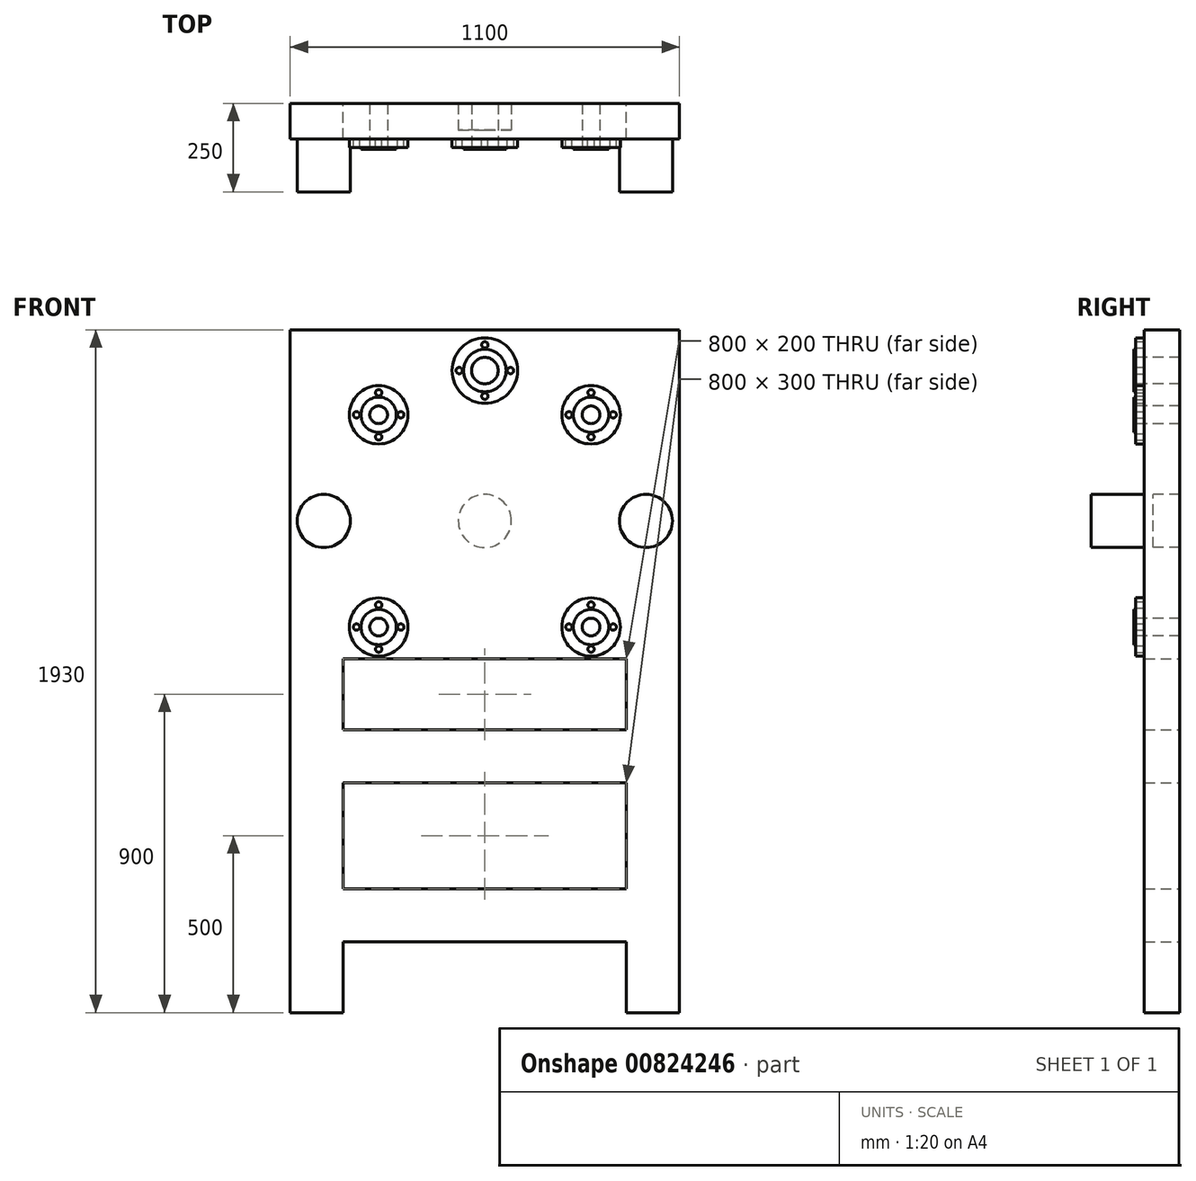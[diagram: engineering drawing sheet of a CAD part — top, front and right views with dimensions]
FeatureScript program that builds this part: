
annotation { "Feature Type Name" : "Feature", "Feature Type Description" : "" }
export const myFeature = defineFeature(function(context is Context, id is Id, definition is map)
    precondition{}
    {
        {
            var Q0;
            Q0=qCreatedBy(makeId("Front.planeOp"),FACE);
            var sketch = newSketch(context, id + "F0", { "sketchPlane" : qUnion([Q0])});
            skLineSegment(sketch, "E0.bottom", {"start": v(550, -965) * mm, "end": v(400, -965) * mm});
            skLineSegment(sketch, "E0.top", {"start": v(550, 965) * mm, "end": v(-550, 965) * mm});
            skLineSegment(sketch, "E0.left", {"start": v(550, -965) * mm, "end": v(550, 965) * mm});
            skLineSegment(sketch, "E0.right", {"start": v(-550, -965) * mm, "end": v(-550, 965) * mm});
            skPoint(sketch, "E0.middle", {"position": v(0, 0) * mm});
            skLineSegment(sketch, "E1.top", {"start": v(-400, -765) * mm, "end": v(400, -765) * mm});
            skLineSegment(sketch, "E1.left", {"start": v(-400, -965) * mm, "end": v(-400, -765) * mm});
            skLineSegment(sketch, "E1.right", {"start": v(400, -965) * mm, "end": v(400, -765) * mm});
            skLineSegment(sketch, "E2.bottom", {"start": v(-400, -615) * mm, "end": v(400, -615) * mm});
            skLineSegment(sketch, "E2.top", {"start": v(-400, -315) * mm, "end": v(400, -315) * mm});
            skLineSegment(sketch, "E2.left", {"start": v(-400, -615) * mm, "end": v(-400, -315) * mm});
            skLineSegment(sketch, "E2.right", {"start": v(400, -615) * mm, "end": v(400, -315) * mm});
            skLineSegment(sketch, "E3.trimOffspring", {"start": v(-400, -965) * mm, "end": v(-550, -965) * mm});
            skLineSegment(sketch, "E4.bottom", {"start": v(-400, -165) * mm, "end": v(400, -165) * mm});
            skLineSegment(sketch, "E4.top", {"start": v(-400, 35) * mm, "end": v(400, 35) * mm});
            skLineSegment(sketch, "E4.left", {"start": v(-400, -165) * mm, "end": v(-400, 35) * mm});
            skLineSegment(sketch, "E4.right", {"start": v(400, -165) * mm, "end": v(400, 35) * mm});
            skPoint(sketch, "E5.middle", {"position": v(0, 425) * mm});
            skSolve(sketch);
        }
        {
            var Q0;
            Q0=makeQuery(id+"F0.imprint","IMPRINT",FACE,{"disambiguationData":[TD([[makeQuery(id+"F0.imprint","IMPRINT",EDGE,{"derivedFrom":sQuery(id+"F0.wireOp",EDGE,"E0.bottom")}),-1.0]])]});
            extrude(context, id + "F1", {"entities" : qUnion([Q0]), "depth" : 100 * mm, "offsetDistance" : 25 * mm});
        }
        {
            var Q0;
            Q0=makeQuery(id+"F1.opExtrude","CAP_FACE",FACE,{"disambiguationData":[OSD([sQuery(id+"F0.wireOp",EDGE,"E0.bottom"),sQuery(id+"F0.wireOp",EDGE,"E0.top"),sQuery(id+"F0.wireOp",EDGE,"E0.left"),sQuery(id+"F0.wireOp",EDGE,"E0.right"),sQuery(id+"F0.wireOp",EDGE,"E1.top"),sQuery(id+"F0.wireOp",EDGE,"E1.left"),sQuery(id+"F0.wireOp",EDGE,"E1.right"),sQuery(id+"F0.wireOp",EDGE,"E2.bottom"),sQuery(id+"F0.wireOp",EDGE,"E2.top"),sQuery(id+"F0.wireOp",EDGE,"E2.left"),sQuery(id+"F0.wireOp",EDGE,"E2.right"),sQuery(id+"F0.wireOp",EDGE,"E3.trimOffspring"),sQuery(id+"F0.wireOp",EDGE,"nSGubIzk-R7de-6MO4-penA-cvBglKJnvsGC"),sQuery(id+"F0.wireOp",EDGE,"E4.bottom"),sQuery(id+"F0.wireOp",EDGE,"E4.top"),sQuery(id+"F0.wireOp",EDGE,"E4.left"),sQuery(id+"F0.wireOp",EDGE,"E4.right")])],"isStart":false});
            var sketch = newSketch(context, id + "F2", { "sketchPlane" : qUnion([Q0])});
            skCircle(sketch, "E6", {"center": v(-300, 125) * mm, "radius": 25 * mm});
            skCircle(sketch, "E7.0", {"center": v(0, 425) * mm, "radius": 75 * mm});
            skCircle(sketch, "E8.0.1.0", {"center": v(-300, 725) * mm, "radius": 25 * mm});
            skCircle(sketch, "E8.1.0.0", {"center": v(300, 125) * mm, "radius": 25 * mm});
            skCircle(sketch, "E8.1.1.0", {"center": v(300, 725) * mm, "radius": 25 * mm});
            skLineSegment(sketch, "E8.direction1", {"start": v(-300, 125) * mm, "end": v(300, 125) * mm, "construction": true});
            skLineSegment(sketch, "E8.direction2", {"start": v(-300, 125) * mm, "end": v(-300, 725) * mm, "construction": true});
            skSolve(sketch);
        }
        {
            var Q0;
            Q0 = qSketchRegion(id + "F2", true);
            extrude(context, id + "F3", {"entities" : qUnion([Q0]), "operationType" : NewBodyOperationType.REMOVE, "oppositeDirection" : true, "depth" : 100 * mm, "offsetDistance" : 25 * mm});
        }
        {
            var Q0;
            Q0=makeQuery(id+"F1.opExtrude","CAP_FACE",FACE,{"disambiguationData":[OSD([sQuery(id+"F0.wireOp",EDGE,"E0.bottom"),sQuery(id+"F0.wireOp",EDGE,"E0.top"),sQuery(id+"F0.wireOp",EDGE,"E0.left"),sQuery(id+"F0.wireOp",EDGE,"E0.right"),sQuery(id+"F0.wireOp",EDGE,"E1.top"),sQuery(id+"F0.wireOp",EDGE,"E1.left"),sQuery(id+"F0.wireOp",EDGE,"E1.right"),sQuery(id+"F0.wireOp",EDGE,"E2.bottom"),sQuery(id+"F0.wireOp",EDGE,"E2.top"),sQuery(id+"F0.wireOp",EDGE,"E2.left"),sQuery(id+"F0.wireOp",EDGE,"E2.right"),sQuery(id+"F0.wireOp",EDGE,"E3.trimOffspring"),sQuery(id+"F0.wireOp",EDGE,"nSGubIzk-R7de-6MO4-penA-cvBglKJnvsGC"),sQuery(id+"F0.wireOp",EDGE,"E4.bottom"),sQuery(id+"F0.wireOp",EDGE,"E4.top"),sQuery(id+"F0.wireOp",EDGE,"E4.left"),sQuery(id+"F0.wireOp",EDGE,"E4.right")])],"isStart":false});
            var sketch = newSketch(context, id + "F4", { "sketchPlane" : qUnion([Q0])});
            skCircle(sketch, "E9", {"center": v(-455, 425) * mm, "radius": 75 * mm});
            skCircle(sketch, "E10.MirrorC", {"center": v(455, 425) * mm, "radius": 75 * mm});
            skSolve(sketch);
        }
        {
            var Q0;
            Q0 = qSketchRegion(id + "F4", true);
            extrude(context, id + "F5", {"entities" : qUnion([Q0]), "operationType" : NewBodyOperationType.ADD, "depth" : 150 * mm, "offsetDistance" : 25 * mm});
        }
        {
            var Q0;
            Q0=makeQuery(id+"F1.opExtrude","CAP_FACE",FACE,{"disambiguationData":[OSD([sQuery(id+"F0.wireOp",EDGE,"E0.bottom"),sQuery(id+"F0.wireOp",EDGE,"E0.top"),sQuery(id+"F0.wireOp",EDGE,"E0.left"),sQuery(id+"F0.wireOp",EDGE,"E0.right"),sQuery(id+"F0.wireOp",EDGE,"E1.top"),sQuery(id+"F0.wireOp",EDGE,"E1.left"),sQuery(id+"F0.wireOp",EDGE,"E1.right"),sQuery(id+"F0.wireOp",EDGE,"E2.bottom"),sQuery(id+"F0.wireOp",EDGE,"E2.top"),sQuery(id+"F0.wireOp",EDGE,"E2.left"),sQuery(id+"F0.wireOp",EDGE,"E2.right"),sQuery(id+"F0.wireOp",EDGE,"E3.trimOffspring"),sQuery(id+"F0.wireOp",EDGE,"nSGubIzk-R7de-6MO4-penA-cvBglKJnvsGC"),sQuery(id+"F0.wireOp",EDGE,"E4.bottom"),sQuery(id+"F0.wireOp",EDGE,"E4.top"),sQuery(id+"F0.wireOp",EDGE,"E4.left"),sQuery(id+"F0.wireOp",EDGE,"E4.right")])],"isStart":false});
            var sketch = newSketch(context, id + "F6", { "sketchPlane" : qUnion([Q0])});
            skCircle(sketch, "E11", {"center": v(-300, 725) * mm, "radius": 82.5 * mm});
            skCircle(sketch, "E12", {"center": v(-300, 787.5) * mm, "radius": 9 * mm});
            skCircle(sketch, "E13.0", {"center": v(-300, 725) * mm, "radius": 25 * mm});
            skCircle(sketch, "E14.1.0", {"center": v(-362.5, 725) * mm, "radius": 9 * mm});
            skCircle(sketch, "E14.2.0", {"center": v(-300, 662.5) * mm, "radius": 9 * mm});
            skCircle(sketch, "E14.3.0", {"center": v(-237.5, 725) * mm, "radius": 9 * mm});
            skPoint(sketch, "E15.0.1.0", {"position": v(-300, 125) * mm});
            skCircle(sketch, "E15.0.1.1", {"center": v(-300, 125) * mm, "radius": 82.5 * mm});
            skCircle(sketch, "E15.0.1.2", {"center": v(-300, 125) * mm, "radius": 25 * mm});
            skCircle(sketch, "E15.0.1.3", {"center": v(-237.5, 125) * mm, "radius": 9 * mm});
            skCircle(sketch, "E15.0.1.4", {"center": v(-362.5, 125) * mm, "radius": 9 * mm});
            skCircle(sketch, "E15.0.1.5", {"center": v(-300, 187.5) * mm, "radius": 9 * mm});
            skCircle(sketch, "E15.0.1.6", {"center": v(-300, 62.5) * mm, "radius": 9 * mm});
            skPoint(sketch, "E15.1.0.0", {"position": v(300, 725) * mm});
            skCircle(sketch, "E15.1.0.1", {"center": v(300, 725) * mm, "radius": 82.5 * mm});
            skCircle(sketch, "E15.1.0.2", {"center": v(300, 725) * mm, "radius": 25 * mm});
            skCircle(sketch, "E15.1.0.3", {"center": v(362.5, 725) * mm, "radius": 9 * mm});
            skCircle(sketch, "E15.1.0.4", {"center": v(237.5, 725) * mm, "radius": 9 * mm});
            skCircle(sketch, "E15.1.0.5", {"center": v(300, 787.5) * mm, "radius": 9 * mm});
            skCircle(sketch, "E15.1.0.6", {"center": v(300, 662.5) * mm, "radius": 9 * mm});
            skPoint(sketch, "E15.1.1.0", {"position": v(300, 125) * mm});
            skCircle(sketch, "E15.1.1.1", {"center": v(300, 125) * mm, "radius": 82.5 * mm});
            skCircle(sketch, "E15.1.1.2", {"center": v(300, 125) * mm, "radius": 25 * mm});
            skCircle(sketch, "E15.1.1.3", {"center": v(362.5, 125) * mm, "radius": 9 * mm});
            skCircle(sketch, "E15.1.1.4", {"center": v(237.5, 125) * mm, "radius": 9 * mm});
            skCircle(sketch, "E15.1.1.5", {"center": v(300, 187.5) * mm, "radius": 9 * mm});
            skCircle(sketch, "E15.1.1.6", {"center": v(300, 62.5) * mm, "radius": 9 * mm});
            skLineSegment(sketch, "E15.direction1", {"start": v(-300, 662.5) * mm, "end": v(300, 662.5) * mm, "construction": true});
            skLineSegment(sketch, "E15.direction2", {"start": v(-300, 662.5) * mm, "end": v(-300, 62.5) * mm, "construction": true});
            skSolve(sketch);
        }
        {
            var Q0;
            Q0 = qSketchRegion(id + "F6", true);
            extrude(context, id + "F7", {"entities" : qUnion([Q0]), "operationType" : NewBodyOperationType.ADD, "depth" : 25 * mm, "offsetDistance" : 25 * mm});
        }
        {
            var Q0;
            Q0=makeQuery(id+"F7.opExtrude","CAP_FACE",FACE,{"disambiguationData":[OSD([sQuery(id+"F6.wireOp",EDGE,"E11"),sQuery(id+"F6.wireOp",EDGE,"E12"),sQuery(id+"F6.wireOp",EDGE,"E13.0"),sQuery(id+"F6.wireOp",EDGE,"E14.1.0"),sQuery(id+"F6.wireOp",EDGE,"E14.2.0"),sQuery(id+"F6.wireOp",EDGE,"E14.3.0")])],"isStart":false});
            var sketch = newSketch(context, id + "F8", { "sketchPlane" : qUnion([Q0])});
            skCircle(sketch, "E16", {"center": v(-300, 725) * mm, "radius": 50 * mm});
            skCircle(sketch, "E17.0.1.0", {"center": v(-300, 125) * mm, "radius": 50 * mm});
            skCircle(sketch, "E17.1.0.0", {"center": v(300, 725) * mm, "radius": 50 * mm});
            skCircle(sketch, "E17.1.1.0", {"center": v(300, 125) * mm, "radius": 50 * mm});
            skLineSegment(sketch, "E17.direction1", {"start": v(-300, 725) * mm, "end": v(300, 725) * mm, "construction": true});
            skLineSegment(sketch, "E17.direction2", {"start": v(-300, 725) * mm, "end": v(-300, 125) * mm, "construction": true});
            skCircle(sketch, "E18", {"center": v(300, 725) * mm, "radius": 25 * mm});
            skCircle(sketch, "E19", {"center": v(300, 125) * mm, "radius": 25 * mm});
            skCircle(sketch, "E20", {"center": v(-300, 125) * mm, "radius": 25 * mm});
            skCircle(sketch, "E21", {"center": v(-300, 725) * mm, "radius": 25 * mm});
            skSolve(sketch);
        }
        {
            var Q0;
            Q0 = qSketchRegion(id + "F8", true);
            extrude(context, id + "F9", {"entities" : qUnion([Q0]), "operationType" : NewBodyOperationType.ADD, "depth" : 5 * mm, "offsetDistance" : 25 * mm});
        }
        {
            var Q0;
            {var subQ0=sQuery(id+"F0.wireOp",EDGE,"E4.right");var subQ1=sQuery(id+"F0.wireOp",EDGE,"E4.left");var subQ2=sQuery(id+"F0.wireOp",EDGE,"E4.top");var subQ3=sQuery(id+"F0.wireOp",EDGE,"E1.left");var subQ4=sQuery(id+"F0.wireOp",EDGE,"E4.bottom");var subQ5=sQuery(id+"F0.wireOp",EDGE,"E3.trimOffspring");var subQ6=sQuery(id+"F0.wireOp",EDGE,"E2.right");var subQ7=sQuery(id+"F0.wireOp",EDGE,"E0.left");var subQ8=sQuery(id+"F0.wireOp",EDGE,"E0.top");var subQ9=sQuery(id+"F0.wireOp",EDGE,"E0.right");var subQ10=sQuery(id+"F0.wireOp",EDGE,"E2.bottom");var subQ11=sQuery(id+"F0.wireOp",EDGE,"E0.bottom");var subQ12=sQuery(id+"F0.wireOp",EDGE,"E2.left");var subQ13=sQuery(id+"F0.wireOp",EDGE,"E1.top");var subQ14=sQuery(id+"F0.wireOp",EDGE,"E1.right");var subQ15=sQuery(id+"F0.wireOp",EDGE,"E2.top");Q0=makeQuery(id+"F7.boolean.opBoolean","SPLIT",FACE,{"disambiguationData":[TD([makeQuery(id+"F1.opExtrude","SWEPT_FACE",FACE,{"disambiguationData":[OSD([subQ11])]})])],"derivedFrom":makeQuery(id+"F1.opExtrude","CAP_FACE",FACE,{"disambiguationData":[OSD([subQ11,subQ8,subQ7,subQ9,subQ13,subQ3,subQ14,subQ10,subQ15,subQ12,subQ6,subQ5,subQ4,subQ2,subQ1,subQ0])],"isStart":false})});}
            var sketch = newSketch(context, id + "F10", { "sketchPlane" : qUnion([Q0])});
            skCircle(sketch, "E22.0", {"center": v(0, 425) * mm, "radius": 75 * mm});
            skSolve(sketch);
        }
        {
            var Q0;
            Q0 = qSketchRegion(id + "F10", true);
            extrude(context, id + "F11", {"entities" : qUnion([Q0]), "operationType" : NewBodyOperationType.ADD, "oppositeDirection" : true, "depth" : 25 * mm, "offsetDistance" : 25 * mm});
        }
        {
            var Q0;
            {var subQ0=sQuery(id+"F0.wireOp",EDGE,"E4.right");var subQ1=sQuery(id+"F0.wireOp",EDGE,"E4.left");var subQ2=sQuery(id+"F0.wireOp",EDGE,"E4.top");var subQ3=sQuery(id+"F0.wireOp",EDGE,"E1.left");var subQ4=sQuery(id+"F0.wireOp",EDGE,"E4.bottom");var subQ5=sQuery(id+"F0.wireOp",EDGE,"E3.trimOffspring");var subQ6=sQuery(id+"F0.wireOp",EDGE,"E2.right");var subQ7=sQuery(id+"F0.wireOp",EDGE,"E0.left");var subQ8=sQuery(id+"F0.wireOp",EDGE,"E0.top");var subQ9=sQuery(id+"F0.wireOp",EDGE,"E0.right");var subQ10=sQuery(id+"F0.wireOp",EDGE,"E2.bottom");var subQ11=sQuery(id+"F0.wireOp",EDGE,"E0.bottom");var subQ12=sQuery(id+"F0.wireOp",EDGE,"E2.left");var subQ13=sQuery(id+"F0.wireOp",EDGE,"E1.top");var subQ14=sQuery(id+"F0.wireOp",EDGE,"E1.right");var subQ15=sQuery(id+"F0.wireOp",EDGE,"E2.top");Q0=makeQuery(id+"F11.boolean.opBoolean","MERGE",FACE,{"derivedFrom":[makeQuery(id+"F7.boolean.opBoolean","SPLIT",FACE,{"disambiguationData":[TD([makeQuery(id+"F1.opExtrude","SWEPT_FACE",FACE,{"disambiguationData":[OSD([subQ11])]})])],"derivedFrom":makeQuery(id+"F1.opExtrude","CAP_FACE",FACE,{"disambiguationData":[OSD([subQ11,subQ8,subQ7,subQ9,subQ13,subQ3,subQ14,subQ10,subQ15,subQ12,subQ6,subQ5,subQ4,subQ2,subQ1,subQ0])],"isStart":false})}),makeQuery(id+"F11.opExtrude","CAP_FACE",FACE,{"disambiguationData":[OSD([sQuery(id+"F10.wireOp",EDGE,"E22.0")])],"isStart":true})]});}
            var sketch = newSketch(context, id + "F12", { "sketchPlane" : qUnion([Q0])});
            skCircle(sketch, "E23", {"center": v(0, 850) * mm, "radius": 37.5 * mm});
            skPoint(sketch, "E23.centerSnap0", {"position": v(0, 965) * mm});
            skCircle(sketch, "E24.0", {"center": v(300, 725) * mm, "radius": 25 * mm});
            skSolve(sketch);
        }
        {
            var Q0;
            Q0=makeQuery(id+"F12.imprint","IMPRINT",FACE,{"disambiguationData":[TD([[makeQuery(id+"F12.imprint","IMPRINT",EDGE,{"derivedFrom":sQuery(id+"F12.wireOp",EDGE,"E23")}),1.0]])]});
            extrude(context, id + "F13", {"entities" : qUnion([Q0]), "operationType" : NewBodyOperationType.REMOVE, "oppositeDirection" : true, "depth" : 100 * mm, "offsetDistance" : 25 * mm});
        }
        {
            var Q0;
            {var subQ0=sQuery(id+"F0.wireOp",EDGE,"E4.right");var subQ1=sQuery(id+"F0.wireOp",EDGE,"E4.left");var subQ2=sQuery(id+"F0.wireOp",EDGE,"E4.top");var subQ3=sQuery(id+"F0.wireOp",EDGE,"E1.left");var subQ4=sQuery(id+"F0.wireOp",EDGE,"E4.bottom");var subQ5=sQuery(id+"F0.wireOp",EDGE,"E3.trimOffspring");var subQ6=sQuery(id+"F0.wireOp",EDGE,"E2.right");var subQ7=sQuery(id+"F0.wireOp",EDGE,"E0.left");var subQ8=sQuery(id+"F0.wireOp",EDGE,"E0.top");var subQ9=sQuery(id+"F0.wireOp",EDGE,"E0.right");var subQ10=sQuery(id+"F0.wireOp",EDGE,"E2.bottom");var subQ11=sQuery(id+"F0.wireOp",EDGE,"E0.bottom");var subQ12=sQuery(id+"F0.wireOp",EDGE,"E2.left");var subQ13=sQuery(id+"F0.wireOp",EDGE,"E1.top");var subQ14=sQuery(id+"F0.wireOp",EDGE,"E1.right");var subQ15=sQuery(id+"F0.wireOp",EDGE,"E2.top");Q0=makeQuery(id+"F11.boolean.opBoolean","MERGE",FACE,{"derivedFrom":[makeQuery(id+"F7.boolean.opBoolean","SPLIT",FACE,{"disambiguationData":[TD([makeQuery(id+"F1.opExtrude","SWEPT_FACE",FACE,{"disambiguationData":[OSD([subQ11])]})])],"derivedFrom":makeQuery(id+"F1.opExtrude","CAP_FACE",FACE,{"disambiguationData":[OSD([subQ11,subQ8,subQ7,subQ9,subQ13,subQ3,subQ14,subQ10,subQ15,subQ12,subQ6,subQ5,subQ4,subQ2,subQ1,subQ0])],"isStart":false})}),makeQuery(id+"F11.opExtrude","CAP_FACE",FACE,{"disambiguationData":[OSD([sQuery(id+"F10.wireOp",EDGE,"E22.0")])],"isStart":true})]});}
            var sketch = newSketch(context, id + "F14", { "sketchPlane" : qUnion([Q0])});
            skCircle(sketch, "E25", {"center": v(0, 850) * mm, "radius": 92.5 * mm});
            skCircle(sketch, "E26", {"center": v(0, 922.5) * mm, "radius": 9 * mm});
            skCircle(sketch, "E27.1.0", {"center": v(-72.5, 850) * mm, "radius": 9 * mm});
            skCircle(sketch, "E27.2.0", {"center": v(0, 777.5) * mm, "radius": 9 * mm});
            skCircle(sketch, "E27.3.0", {"center": v(72.5, 850) * mm, "radius": 9 * mm});
            skSolve(sketch);
        }
        {
            var Q0;
            Q0=makeQuery(id+"F14.imprint","IMPRINT",FACE,{"disambiguationData":[TD([[makeQuery(id+"F14.imprint","IMPRINT",EDGE,{"derivedFrom":sQuery(id+"F14.wireOp",EDGE,"E25")}),1.0]])]});
            extrude(context, id + "F15", {"entities" : qUnion([Q0]), "operationType" : NewBodyOperationType.ADD, "depth" : 25 * mm, "offsetDistance" : 25 * mm});
        }
        {
            var Q0;
            Q0=makeQuery(id+"F15.opExtrude","CAP_FACE",FACE,{"disambiguationData":[OSD([sQuery(id+"F12.wireOp",EDGE,"E23"),sQuery(id+"F14.wireOp",EDGE,"E25"),sQuery(id+"F14.wireOp",EDGE,"E26"),sQuery(id+"F14.wireOp",EDGE,"E27.1.0"),sQuery(id+"F14.wireOp",EDGE,"E27.2.0"),sQuery(id+"F14.wireOp",EDGE,"E27.3.0")])],"isStart":false});
            var sketch = newSketch(context, id + "F16", { "sketchPlane" : qUnion([Q0])});
            skCircle(sketch, "E28", {"center": v(0, 850) * mm, "radius": 60 * mm});
            skSolve(sketch);
        }
        {
            var Q0;
            Q0=makeQuery(id+"F16.imprint","IMPRINT",FACE,{"disambiguationData":[TD([[makeQuery(id+"F16.imprint","IMPRINT",EDGE,{"derivedFrom":sQuery(id+"F16.wireOp",EDGE,"E28")}),1.0]])]});
            extrude(context, id + "F17", {"entities" : qUnion([Q0]), "operationType" : NewBodyOperationType.ADD, "depth" : 5 * mm, "offsetDistance" : 25 * mm});
        }
    });
